# Revit family: Sanitary_Installation-Systems_hansgrohe_15313XXX-RainSelect-Basic-set-for-5-func
name_source: partatom
category: Plumbing Fixtures
revit_build: Autodesk Revit 2018 (Build: 20190510_1515(x64)
units: mm (PartAtom-declared; Revit-internal decimal feet)

## family parameters
Always vertical = No
Cut with Voids When Loaded = No
OmniClass Number = 23.27.31.29.11
OmniClass Title = Manual Mixing Valves
Part Type = Normal
Room Calculation Point = No
Round Connector Dimension = Use Diameter
Shared = No
Work Plane-Based = Yes

## types (1)
- 15313XXX RainSelect Basic set for 5 functions
    Always visible = Yes
    BIMobject category = Installation Systems
    Default Elevation = 1219.2 mm
    Description = RainSelect Basic set for 5 functions
    Diameter = 19 mm
    Edition number = 1
    IFC Classification = Sanitary Terminal
    Important Note = Premixed water outlets 2 to 5 can be either at the top OR at the bottom of this product. No two connectors with the same name are to be used simultaneously.
    Manufacturer = Hansgrohe
    Manufacturer name = hansgrohe
    Material 1 = Hansgrohe - Metal - Brass
    Material 2 = Hansgrohe - Plastic - Black
    Material 3 = Hansgrohe - Plastic - Green
    Material 4 = Hansgrohe - Plastic - Gray
    Model = 15313XXX
    OmniClass Code = 23-27 31 29 11
    OmniClass Description = Manual Mixing Valves
    Outlet Diameter = 13 mm
    Product Guid = 3af59678-dfba-44c2-ac70-54b7297cc1f0
    Product SKU = 15313XXX
    Product data url = https://bimobject.com
    Product family = RainSelect
    Product group = Concealed Basic set bath/shower mixers
    Product name = 15313XXX RainSelect Basic set for 5 functions
    Product url = https://www.hansgrohe.com
    QR code = https://bimobject.com
    URL = https://www.hansgrohe.com
    Weight Net (Kg) = 6,9

## geometry (parser evidence)
native form markers: Sweep x2
no freeform markers — native parametric forms only
